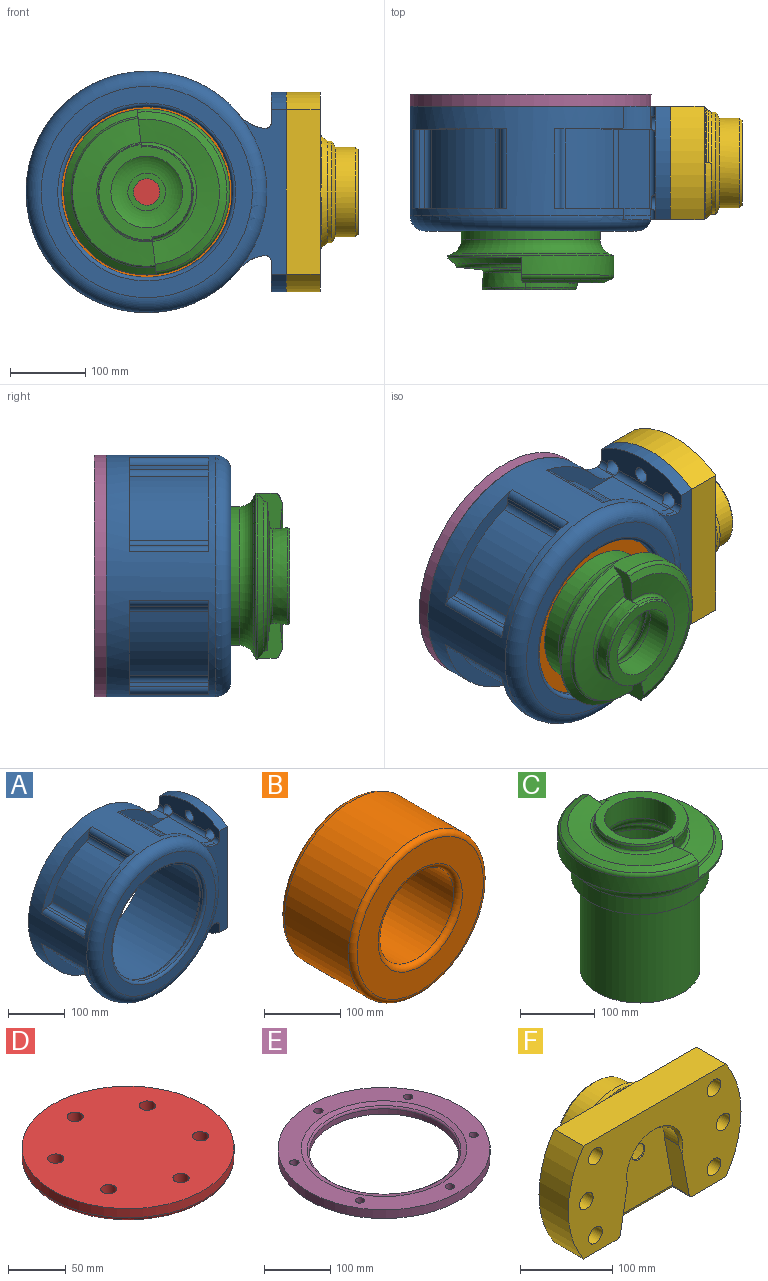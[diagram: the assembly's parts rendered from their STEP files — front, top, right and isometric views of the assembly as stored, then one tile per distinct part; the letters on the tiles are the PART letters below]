
ASSEMBLY  parts=6 mates=13
PART A: 99 faces, bbox 381.5x168.7x349.7 mm
  f0: cylinder r=30mm len=60mm, axis (1,0,0), area 6597.3mm2, adj f6,f71
  f1: plane 265x150mm, normal (1,0,0), area 30406.7mm2, adj f7,f8,f38,f39,f40,f61,f63,f65
  f2: plane 150x40.5mm, normal (-1,0,0), area 4307.7mm2, adj f4,f7,f8,f39,f65,f67,f70
  f3: plane 150x40.5mm, normal (-1,0,0), area 4307.7mm2, adj f5,f7,f8,f38,f61,f63,f69
  f4: cylinder r=8mm len=150mm, axis (0,-1,0), area 1467.6mm2, adj f2,f7,f8,f11,f12,f36,f41,f42
  f5: cylinder r=8mm len=150mm, axis (0,1,0), area 1467.6mm2, adj f3,f7,f8,f23,f24,f37,f44,f45
  f6: plane 80x80mm, normal (1,0,0), area 2199.1mm2, adj f0,f40
  f7: plane 345x320mm, normal (0,1,0), area 36954.8mm2, adj f1,f2,f3,f4,f5,f10,f14,f38
  f8: plane 221.75x66.5mm, normal (0,-1,0), area 6828.4mm2, adj f1,f2,f3,f4,f5,f13,f38,f39
  f9: cylinder r=140mm len=105mm, axis (0,1,0), area 8139.3mm2, adj f23,f24,f47,f53
  f10: cylinder r=160mm len=320mm, axis (0,1,0), area 51651.4mm2, adj f7,f11,f12,f13,f18,f19,f23,f24
  f11: plane 126.34x72.77mm, normal (0,1,0), area 2207.3mm2, adj f4,f10,f20,f21,f36,f43,f48,f55
  f12: plane 126.34x72.77mm, normal (0,-1,0), area 2207.3mm2, adj f4,f10,f20,f21,f36,f41,f48,f55
  f13: torus R=140mm, axis (0,1,0), area 29023.4mm2, adj f8,f10,f33,f42,f45
  f14: cylinder r=125mm len=250mm, axis (0,1,0), area 114668.1mm2, adj f7,f35
  f15: plane 105x5.55mm, normal (-1,0,0), area 582.5mm2, adj f18,f19,f57,f60
  f16: plane 105x5.55mm, normal (0,0,-1), area 582.5mm2, adj f18,f19,f58,f59
  f17: cylinder r=140mm len=105mm, axis (0,1,0), area 13099.5mm2, adj f18,f19,f59,f60
  f18: plane 124.77x124.77mm, normal (0,1,0), area 3098.8mm2, adj f10,f15,f16,f17,f57,f58,f59,f60
  f19: plane 124.77x124.77mm, normal (0,-1,0), area 3098.8mm2, adj f10,f15,f16,f17,f57,f58,f59,f60
  f20: cylinder r=140mm len=105mm, axis (0,1,0), area 8139.3mm2, adj f11,f12,f48,f56
  f21: plane 105x5.55mm, normal (1,0,0), area 582.5mm2, adj f11,f12,f55,f56
  f22: plane 105x5.55mm, normal (1,0,0), area 582.5mm2, adj f23,f24,f53,f54
  f23: plane 126.34x72.77mm, normal (0,1,0), area 2207.3mm2, adj f5,f9,f10,f22,f37,f46,f47,f53
  f24: plane 126.34x72.77mm, normal (0,-1,0), area 2207.3mm2, adj f5,f9,f10,f22,f37,f44,f47,f53
  f25: plane 105x5.55mm, normal (0,0,1), area 582.5mm2, adj f28,f29,f49,f52
  f26: plane 105x5.55mm, normal (-1,0,0), area 582.5mm2, adj f28,f29,f50,f51
  f27: cylinder r=140mm len=105mm, axis (0,1,0), area 13099.5mm2, adj f28,f29,f51,f52
  f28: plane 124.77x124.77mm, normal (0,1,0), area 3098.8mm2, adj f10,f25,f26,f27,f49,f50,f51,f52
  f29: plane 124.77x124.77mm, normal (0,-1,0), area 3098.8mm2, adj f10,f25,f26,f27,f49,f50,f51,f52
  f30: cylinder r=113mm len=226mm, axis (0,1,0), area 4260mm2, adj f31,f34
  f31: torus R=117mm, axis (0,1,0), area 4518.4mm2, adj f30,f32
  f32: plane 242x242mm, normal (0,1,0), area 2990.8mm2, adj f31,f35
  f33: plane 280x280mm, normal (0,-1,0), area 17831.7mm2, adj f13,f34
  f34: torus R=118mm, axis (0,1,0), area 5666mm2, adj f30,f33
  f35: torus R=121mm, axis (0,-1,0), area 4877.4mm2, adj f14,f32
  f36: plane 105x40.11mm, normal (0,0,-1), area 4211.2mm2, adj f4,f11,f12,f48
  f37: plane 105x40.11mm, normal (0,0,1), area 4211.2mm2, adj f5,f23,f24,f47
  f38: cylinder r=132.5mm len=150mm, axis (1,0,0), area 3189mm2, adj f1,f3,f7,f8
  f39: cylinder r=132.5mm len=150mm, axis (1,0,0), area 3189mm2, adj f1,f2,f7,f8
  f40: cylinder r=40mm len=80mm, axis (1,0,0), area 5026.5mm2, adj f1,f6
  f41: cylinder r=50mm len=35.14mm, axis (0,1,0), area 1217.5mm2, adj f4,f7,f10,f12
  f42: bspline ~40.41x26.95mm, area 251.6mm2, adj f4,f8,f13,f43
  f43: cylinder r=50mm len=35.14mm, axis (0,1,0), area 405.8mm2, adj f4,f10,f11,f42
  f44: cylinder r=50mm len=35.14mm, axis (0,1,0), area 1217.5mm2, adj f5,f7,f10,f24
  f45: bspline ~40.41x26.95mm, area 251.6mm2, adj f5,f8,f13,f46
  f46: cylinder r=50mm len=35.14mm, axis (0,1,0), area 405.8mm2, adj f5,f10,f23,f45
  f47: cylinder r=10mm len=105mm, axis (0,1,0), area 938.2mm2, adj f9,f23,f24,f37
  f48: cylinder r=10mm len=105mm, axis (0,1,0), area 938.2mm2, adj f11,f12,f20,f36
  f49: cylinder r=10mm len=105mm, axis (0,1,0), area 1437.9mm2, adj f10,f25,f28,f29
  f50: cylinder r=10mm len=105mm, axis (0,1,0), area 1437.9mm2, adj f10,f26,f28,f29
  f51: cylinder r=10mm len=105mm, axis (0,1,0), area 1292.5mm2, adj f26,f27,f28,f29
  f52: cylinder r=10mm len=105mm, axis (0,1,0), area 1292.5mm2, adj f25,f27,f28,f29
  f53: cylinder r=10mm len=105mm, axis (0,1,0), area 1292.5mm2, adj f9,f22,f23,f24
  f54: cylinder r=10mm len=105mm, axis (0,1,0), area 1437.9mm2, adj f10,f22,f23,f24
  f55: cylinder r=10mm len=105mm, axis (0,1,0), area 1437.9mm2, adj f10,f11,f12,f21
  f56: cylinder r=10mm len=105mm, axis (0,1,0), area 1292.5mm2, adj f11,f12,f20,f21
  f57: cylinder r=10mm len=105mm, axis (0,1,0), area 1437.9mm2, adj f10,f15,f18,f19
  f58: cylinder r=10mm len=105mm, axis (0,1,0), area 1437.9mm2, adj f10,f16,f18,f19
  f59: cylinder r=10mm len=105mm, axis (0,1,0), area 1292.5mm2, adj f16,f17,f18,f19
  f60: cylinder r=10mm len=105mm, axis (0,1,0), area 1292.5mm2, adj f15,f17,f18,f19
  f61: cylinder r=10.5mm len=25mm, axis (1,0,0), area 1455.7mm2, adj f1,f3,f5,f62
  f62: plane 16.73x4.15mm, normal (1,0,0), area 48.5mm2, adj f5,f61
  f63: cylinder r=10.5mm len=25mm, axis (1,0,0), area 1455.7mm2, adj f1,f3,f5,f64
  f64: plane 16.73x4.15mm, normal (1,0,0), area 48.5mm2, adj f5,f63
  f65: cylinder r=10.5mm len=25mm, axis (1,0,0), area 1455.7mm2, adj f1,f2,f4,f66
  f66: plane 16.73x4.15mm, normal (1,0,0), area 48.5mm2, adj f4,f65
  f67: cylinder r=10.5mm len=25mm, axis (1,0,0), area 1455.7mm2, adj f1,f2,f4,f68
  f68: plane 16.73x4.15mm, normal (1,0,0), area 48.5mm2, adj f4,f67
  f69: cylinder r=10.5mm len=21mm, axis (1,0,0), area 1319.5mm2, adj f1,f3
  f70: cylinder r=10.5mm len=21mm, axis (1,0,0), area 1319.5mm2, adj f1,f2
  f71: plane 100x80mm, normal (-1,0,0), area 5172.6mm2, adj f0,f74,f75,f79,f80
  f72: cylinder r=10mm len=100mm, axis (0,-1,0), area 1840.7mm2, adj f73,f78,f79,f80
  f73: plane 100x15.43mm, normal (0,0,1), area 1543.2mm2, adj f72,f74,f79,f80
  f74: cylinder r=10mm len=100mm, axis (0,-1,0), area 1570.8mm2, adj f71,f73,f79,f80
  f75: cylinder r=10mm len=100mm, axis (0,-1,0), area 1570.8mm2, adj f71,f76,f79,f80
  f76: plane 100x15.43mm, normal (0,0,-1), area 1543.2mm2, adj f75,f77,f79,f80
  f77: cylinder r=10mm len=100mm, axis (0,-1,0), area 1840.7mm2, adj f76,f78,f79,f80
  f78: cylinder r=140mm len=100mm, axis (0,-1,0), area 7558.1mm2, adj f72,f77,f79,f80
  f79: plane 100x35.43mm, normal (0,-1,0), area 3176.4mm2, adj f71,f72,f73,f74,f75,f76,f77,f78
  f80: plane 100x35.43mm, normal (0,1,0), area 3176.4mm2, adj f71,f72,f73,f74,f75,f76,f77,f78
  f81: cylinder r=6.6mm len=15mm, axis (0,1,0), area 622mm2, adj f82,f83
  f82: cone r=0mm half-angle=59deg, axis (0,1,0), area 159.7mm2, adj f81
  f83: cone r=6.6mm half-angle=45deg, axis (0,1,0), area 63.1mm2, adj f7,f81
  f84: cylinder r=6.6mm len=15mm, axis (0,1,0), area 622mm2, adj f85,f86
  f85: cone r=0mm half-angle=59deg, axis (0,1,0), area 159.7mm2, adj f84
  f86: cone r=6.6mm half-angle=45deg, axis (0,1,0), area 63.1mm2, adj f7,f84
  f87: cylinder r=6.6mm len=15mm, axis (0,1,0), area 622mm2, adj f88,f89
  f88: cone r=0mm half-angle=59deg, axis (0,1,0), area 159.7mm2, adj f87
  f89: cone r=6.6mm half-angle=45deg, axis (0,1,0), area 63.1mm2, adj f7,f87
  f90: cylinder r=6.6mm len=15mm, axis (0,1,0), area 622mm2, adj f91,f92
  f91: cone r=0mm half-angle=59deg, axis (0,1,0), area 159.7mm2, adj f90
  f92: cone r=6.6mm half-angle=45deg, axis (0,1,0), area 63.1mm2, adj f7,f90
  f93: cylinder r=6.6mm len=15mm, axis (0,1,0), area 622mm2, adj f94,f95
  f94: cone r=0mm half-angle=59deg, axis (0,1,0), area 159.7mm2, adj f93
  f95: cone r=6.6mm half-angle=45deg, axis (0,1,0), area 63.1mm2, adj f7,f93
  f96: cylinder r=6.6mm len=15mm, axis (0,1,0), area 622mm2, adj f97,f98
  f97: cone r=0mm half-angle=59deg, axis (0,1,0), area 159.7mm2, adj f96
  f98: cone r=6.6mm half-angle=45deg, axis (0,1,0), area 63.1mm2, adj f7,f96
PART B: 8 faces, bbox 270.6x134x270.6 mm
  f0: cylinder r=70mm len=140mm, axis (0,1,0), area 51899.1mm2, adj f4,f6
  f1: cylinder r=125mm len=250mm, axis (0,1,0), area 92677mm2, adj f5,f7
  f2: plane 234x234mm, normal (0,-1,0), area 23891.8mm2, adj f6,f7
  f3: plane 234x234mm, normal (0,1,0), area 23891.8mm2, adj f4,f5
  f4: torus R=78mm, axis (0,-1,0), area 5756.5mm2, adj f0,f3
  f5: torus R=117mm, axis (0,-1,0), area 9640.1mm2, adj f1,f3
  f6: torus R=78mm, axis (0,-1,0), area 5756.5mm2, adj f0,f2
  f7: torus R=117mm, axis (0,-1,0), area 9640.1mm2, adj f1,f2
PART C: 52 faces, bbox 242.5x242.5x250 mm
  f0: plane 11.85x4.5mm, normal (-1,0,0), area 30.8mm2, adj f2,f43,f45,f46,f49,f50
  f1: plane 11.85x4.5mm, normal (-1,0,0), area 30.8mm2, adj f2,f43,f45,f46,f49,f50
  f2: plane 126.72x123.34mm, normal (0,0,1), area 4869.3mm2, adj f0,f1,f3,f49,f50
  f3: cylinder r=47.5mm len=95mm, axis (0,0,1), area 9960.1mm2, adj f2,f7
  f4: plane 47.43x32.63mm, normal (1,0,0), area 883.5mm2, adj f5,f6,f41,f42,f43,f44,f46,f47
  f5: cone r=62mm half-angle=84.3deg, axis (0,0,-1), area 8363.5mm2, adj f4,f40,f42,f44
  f6: cylinder r=110mm len=220mm, axis (0,0,1), area 9891.7mm2, adj f4,f22,f40,f41,f51
  f7: torus R=63.5mm, axis (0,0,1), area 3876.4mm2, adj f3,f8
  f8: cone r=60.31mm half-angle=45deg, axis (0,0,-1), area 4062.3mm2, adj f7,f9
  f9: torus R=49mm, axis (0,0,1), area 5006.3mm2, adj f8,f10
  f10: cylinder r=65mm len=130mm, axis (0,0,1), area 51407.2mm2, adj f9,f11
  f11: torus R=25mm, axis (0,0,1), area 19922.7mm2, adj f10,f12
  f12: plane 50x50mm, normal (0,0,1), area 1001.4mm2, adj f11,f13
  f13: cylinder r=17.5mm len=35mm, axis (0,0,1), area 2110.7mm2, adj f12,f23
  f14: plane 90x90mm, normal (0,0,-1), area 5041.5mm2, adj f15,f23
  f15: cylinder r=45mm len=90mm, axis (0,0,1), area 1413.7mm2, adj f14,f16
  f16: plane 160x160mm, normal (0,0,-1), area 13067.8mm2, adj f15,f17,f24,f27,f29,f31,f33,f35
  f17: cylinder r=80mm len=160mm, axis (0,0,1), area 73084mm2, adj f16,f18
  f18: torus R=86mm, axis (0,0,1), area 4025.4mm2, adj f17,f19
  f19: cone r=84.45mm half-angle=75deg, axis (0,0,1), area 4334.5mm2, adj f18,f20
  f20: cylinder r=92mm len=184mm, axis (0,0,1), area 14826.9mm2, adj f19,f21
  f21: torus R=112mm, axis (0,0,1), area 13689mm2, adj f20,f22
  f22: cone r=110mm half-angle=65deg, axis (0,0,1), area 4776.3mm2, adj f6,f21
  f23: cone r=20.5mm half-angle=75deg, axis (0,0,-1), area 370.8mm2, adj f13,f14
  f24: cylinder r=5.25mm len=19mm, axis (0,0,-1), area 626.7mm2, adj f16,f25
  f25: cone r=0mm half-angle=59deg, axis (0,0,-1), area 101mm2, adj f24
  f26: cone r=0mm half-angle=59deg, axis (0,0,-1), area 101mm2, adj f27
  f27: cylinder r=5.25mm len=19mm, axis (0,0,-1), area 626.7mm2, adj f16,f26
  f28: cone r=0mm half-angle=59deg, axis (0,0,-1), area 101mm2, adj f29
  f29: cylinder r=5.25mm len=19mm, axis (0,0,-1), area 626.7mm2, adj f16,f28
  f30: cone r=0mm half-angle=59deg, axis (0,0,-1), area 101mm2, adj f31
  f31: cylinder r=5.25mm len=19mm, axis (0,0,-1), area 626.7mm2, adj f16,f30
  f32: cone r=0mm half-angle=59deg, axis (0,0,-1), area 101mm2, adj f33
  f33: cylinder r=5.25mm len=19mm, axis (0,0,-1), area 626.7mm2, adj f16,f32
  f34: cone r=0mm half-angle=59deg, axis (0,0,-1), area 101mm2, adj f35
  f35: cylinder r=5.25mm len=19mm, axis (0,0,-1), area 626.7mm2, adj f16,f34
  f36: cylinder r=5mm len=10mm, axis (0,0,-1), area 314.2mm2, adj f16,f37
  f37: plane 10x10mm, normal (0,0,-1), area 78.5mm2, adj f36
  f38: cylinder r=5mm len=10mm, axis (0,0,-1), area 314.2mm2, adj f16,f39
  f39: plane 10x10mm, normal (0,0,-1), area 78.5mm2, adj f38
  f40: plane 47.43x32.63mm, normal (1,0,0), area 883.5mm2, adj f5,f6,f41,f42,f43,f44,f46,f47
  f41: cone r=110mm half-angle=51deg, axis (0,0,-1), area 4003.1mm2, adj f4,f6,f40,f42
  f42: torus R=104.37mm, axis (0,0,1), area 1633.8mm2, adj f4,f5,f40,f41
  f43: cone r=62.19mm half-angle=5.7deg, axis (0,0,1), area 3814.8mm2, adj f0,f1,f4,f40,f44,f49
  f44: torus R=66.57mm, axis (0,0,1), area 1259mm2, adj f4,f5,f40,f43
  f45: cone r=61.69mm half-angle=5.7deg, axis (0,0,-1), area 1130.6mm2, adj f0,f1,f46,f50
  f46: torus R=65.67mm, axis (0,0,-1), area 1251.3mm2, adj f0,f1,f4,f40,f45,f47
  f47: cone r=66.07mm half-angle=84.3deg, axis (0,0,1), area 7784.9mm2, adj f4,f40,f46,f48
  f48: cone r=110mm half-angle=65.7deg, axis (0,0,-1), area 3513.6mm2, adj f4,f40,f47,f51
  f49: cone r=63.36mm half-angle=19.4deg, axis (0,0,-1), area 683.3mm2, adj f0,f1,f2,f43
  f50: cone r=61.11mm half-angle=20.7deg, axis (0,0,-1), area 607mm2, adj f0,f1,f2,f45
  f51: torus R=104mm, axis (0,0,1), area 2351mm2, adj f4,f6,f40,f48
PART D: 15 faces, bbox 199.2x199.2x16 mm
  f0: cylinder r=45mm len=90mm, axis (0,0,1), area 1131mm2, adj f7,f8
  f1: plane 160x160mm, normal (0,0,-1), area 12242.8mm2, adj f2,f8,f9,f10,f11,f12,f13,f14
  f2: cone r=80mm half-angle=75deg, axis (0,0,1), area 4967.4mm2, adj f1,f3
  f3: torus R=88mm, axis (0,0,1), area 2992.2mm2, adj f2,f4
  f4: cylinder r=92mm len=184mm, axis (0,0,1), area 5616mm2, adj f3,f5
  f5: plane 184x184mm, normal (0,0,1), area 25666.8mm2, adj f4,f9,f10,f11,f12,f13,f14
  f6: plane 86x86mm, normal (0,0,-1), area 5808.8mm2, adj f7
  f7: torus R=43mm, axis (0,0,1), area 873.9mm2, adj f0,f6
  f8: cone r=47mm half-angle=45deg, axis (0,0,-1), area 817.5mm2, adj f0,f1
  f9: cylinder r=7mm len=16mm, axis (0,0,-1), area 703.7mm2, adj f1,f5
  f10: cylinder r=7mm len=16mm, axis (0,0,-1), area 703.7mm2, adj f1,f5
  f11: cylinder r=7mm len=16mm, axis (0,0,-1), area 703.7mm2, adj f1,f5
  f12: cylinder r=7mm len=16mm, axis (0,0,-1), area 703.7mm2, adj f1,f5
  f13: cylinder r=7mm len=16mm, axis (0,0,-1), area 703.7mm2, adj f1,f5
  f14: cylinder r=7mm len=16mm, axis (0,0,-1), area 703.7mm2, adj f1,f5
PART E: 12 faces, bbox 320x320x16 mm
  f0: cylinder r=113mm len=226mm, axis (0,0,1), area 6897.9mm2, adj f1,f5
  f1: plane 320x320mm, normal (0,0,-1), area 39386.1mm2, adj f0,f2,f6,f7,f8,f9,f10,f11
  f2: cylinder r=160mm len=320mm, axis (0,0,1), area 16085mm2, adj f1,f3
  f3: plane 320x320mm, normal (0,0,1), area 30413.8mm2, adj f2,f4,f6,f7,f8,f9,f10,f11
  f4: cone r=125mm half-angle=75deg, axis (0,0,1), area 7081.1mm2, adj f3,f5
  f5: torus R=117mm, axis (0,0,1), area 3752mm2, adj f0,f4
  f6: cylinder r=7mm len=16mm, axis (0,0,1), area 703.7mm2, adj f1,f3
  f7: cylinder r=7mm len=16mm, axis (0,0,1), area 703.7mm2, adj f1,f3
  f8: cylinder r=7mm len=16mm, axis (0,0,1), area 703.7mm2, adj f1,f3
  f9: cylinder r=7mm len=16mm, axis (0,0,1), area 703.7mm2, adj f1,f3
  f10: cylinder r=7mm len=16mm, axis (0,0,1), area 703.7mm2, adj f1,f3
  f11: cylinder r=7mm len=16mm, axis (0,0,1), area 703.7mm2, adj f1,f3
PART F: 56 faces, bbox 265x95x166.1 mm
  f0: cylinder r=10.5mm len=43mm, axis (0,1,0), area 2836.9mm2, adj f13,f44
  f1: cylinder r=10.5mm len=43mm, axis (0,1,0), area 2836.9mm2, adj f13,f43
  f2: cylinder r=10.5mm len=43mm, axis (0,1,0), area 2836.9mm2, adj f13,f40
  f3: plane 150x116.21mm, normal (0,1,0), area 5693.8mm2, adj f6,f8,f12,f27,f30,f33,f46,f48
  f4: cone r=67.5mm half-angle=36.9deg, axis (0,-1,0), area 2247.8mm2, adj f20,f27,f28,f29,f30,f31,f32
  f5: plane 150x116.21mm, normal (0,1,0), area 5693.8mm2, adj f6,f7,f8,f28,f31,f36,f41,f42
  f6: plane 218.46x45mm, normal (0,0,-1), area 6369.9mm2, adj f3,f5,f7,f12,f13,f34,f35,f53
  f7: cylinder r=132.5mm len=150mm, axis (0,1,0), area 7175.2mm2, adj f5,f6,f8,f13
  f8: plane 218.46x45mm, normal (0,0,1), area 9830.7mm2, adj f3,f5,f7,f12,f13,f29,f32
  f9: cylinder r=10.5mm len=43mm, axis (0,1,0), area 2836.9mm2, adj f13,f47
  f10: cylinder r=10.5mm len=43mm, axis (0,1,0), area 2836.9mm2, adj f13,f49
  f11: cylinder r=10.5mm len=43mm, axis (0,1,0), area 2836.9mm2, adj f13,f51
  f12: cylinder r=132.5mm len=150mm, axis (0,1,0), area 7175.2mm2, adj f3,f6,f8,f13
  f13: plane 265x150mm, normal (0,-1,0), area 25475.2mm2, adj f0,f1,f2,f6,f7,f8,f9,f10
  f14: plane 110x105.2mm, normal (0,-1,0), area 8678mm2, adj f15,f16,f17,f52,f55
  f15: cylinder r=40mm len=80mm, axis (0,-1,0), area 2764.6mm2, adj f14,f16,f17,f18
  f16: plane 70.89x25.08mm, normal (0.98,0,-0.18), area 1783.4mm2, adj f13,f14,f15,f18,f53,f55
  f17: plane 70.89x25.08mm, normal (-0.98,0,-0.18), area 1783.4mm2, adj f13,f14,f15,f18,f54,f55
  f18: cone r=40mm half-angle=45deg, axis (0,-1,0), area 601.5mm2, adj f13,f15,f16,f17
  f19: cone r=59.5mm half-angle=60deg, axis (0,-1,0), area 3685.6mm2, adj f20,f23
  f20: cylinder r=67.5mm len=135mm, axis (0,1,0), area 2282.2mm2, adj f4,f19,f24
  f21: cylinder r=49.5mm len=99mm, axis (0,1,0), area 18039mm2, adj f22,f38
  f22: plane 113x113mm, normal (0,1,0), area 2331.1mm2, adj f21,f39
  f23: cylinder r=59.5mm len=119mm, axis (0,1,0), area 10093.9mm2, adj f19,f39
  f24: cone r=67.5mm half-angle=28.1deg, axis (0,-1,0), area 1154.7mm2, adj f20,f25,f27,f28
  f25: torus R=74.87mm, axis (0,-1,0), area 725.6mm2, adj f24,f26,f27,f28
  f26: cone r=75mm half-angle=51.4deg, axis (0,-1,0), area 567.4mm2, adj f25,f27,f28,f33,f34,f35,f36
  f27: plane 10x10mm, normal (0,0,-1), area 8.4mm2, adj f3,f4,f24,f25,f26,f30,f33
  f28: plane 10x10mm, normal (0,0,-1), area 8.4mm2, adj f4,f5,f24,f25,f26,f31,f36
  f29: bspline ~22.8x4.69mm, area 43.3mm2, adj f4,f8,f30
  f30: torus R=77.5mm, axis (0,-1,0), area 459.8mm2, adj f3,f4,f27,f29
  f31: torus R=77.5mm, axis (0,-1,0), area 459.8mm2, adj f4,f5,f28,f32
  f32: bspline ~22.8x4.69mm, area 43.3mm2, adj f4,f8,f31
  f33: torus R=76.75mm, axis (0,-1,0), area 343.1mm2, adj f3,f26,f27,f34
  f34: bspline ~18.64x3.54mm, area 26.6mm2, adj f6,f26,f33
  f35: bspline ~18.64x3.54mm, area 26.6mm2, adj f6,f26,f36
  f36: torus R=76.75mm, axis (0,-1,0), area 343.1mm2, adj f5,f26,f28,f35
  f37: plane 79x79mm, normal (0,1,0), area 4584.4mm2, adj f38,f52
  f38: torus R=39.5mm, axis (0,1,0), area 4526.8mm2, adj f21,f37
  f39: cone r=56.5mm half-angle=45deg, axis (0,-1,0), area 1546.1mm2, adj f22,f23
  f40: plane 40x40mm, normal (0,1,0), area 910.3mm2, adj f2,f41
  f41: cylinder r=20mm len=40mm, axis (0,1,0), area 251.3mm2, adj f5,f40
  f42: cylinder r=20mm len=40mm, axis (0,1,0), area 251.3mm2, adj f5,f43
  f43: plane 40x40mm, normal (0,1,0), area 910.3mm2, adj f1,f42
  f44: plane 40x40mm, normal (0,1,0), area 910.3mm2, adj f0,f45
  f45: cylinder r=20mm len=40mm, axis (0,1,0), area 251.3mm2, adj f5,f44
  f46: cylinder r=20mm len=40mm, axis (0,1,0), area 251.3mm2, adj f3,f47
  f47: plane 40x40mm, normal (0,1,0), area 910.3mm2, adj f9,f46
  f48: cylinder r=20mm len=40mm, axis (0,1,0), area 251.3mm2, adj f3,f49
  f49: plane 40x40mm, normal (0,1,0), area 910.3mm2, adj f10,f48
  f50: cylinder r=20mm len=40mm, axis (0,1,0), area 251.3mm2, adj f3,f51
  f51: plane 40x40mm, normal (0,1,0), area 910.3mm2, adj f11,f50
  f52: cylinder r=10.05mm len=20.1mm, axis (0,1,0), area 126.3mm2, adj f14,f37
  f53: cylinder r=5mm len=30mm, axis (0,-1,0), area 188.3mm2, adj f6,f13,f16,f55
  f54: cylinder r=5mm len=30mm, axis (0,1,0), area 188.3mm2, adj f6,f13,f17,f55
  f55: cylinder r=5mm len=115.36mm, axis (-1,0,0), area 856mm2, adj f6,f14,f16,f17,f53,f54
PLACE A t=(-87.99,-72.92,-63.91)mm fixed
PLACE B rot(axis=(0,-1,0),90deg) t=(-87.99,-80.92,-63.91)mm
PLACE C rot(axis=(0.04,0.71,-0.71),175.3deg) t=(-87.99,9.28,-63.91)mm
PLACE D rot(axis=(-0.23,0.69,0.69),154.3deg) t=(-87.99,1.28,-63.91)mm
PLACE E rot(axis=(0.77,0.45,-0.45),104.5deg) t=(-87.99,18.08,-63.91)mm
PLACE F rot(axis=(0.58,0.58,-0.58),120deg) t=(119.51,-72.92,-63.91)mm
MATE cylindrical C.f3 <-> D.f0  axis (0,-1,0) through (-87.99,6.78,-63.91)mm
MATE planar D.f0 <-> C.f45  axis (0,-1,0) through (-87.99,9.28,-63.91)mm
MATE cylindrical C.f28 <-> D.f12  axis (0,1,0) through (-126.78,-5.22,-11.76)mm
MATE planar E.f0 <-> A.f7  axis (0,-1,0) through (-87.99,2.08,-63.91)mm
MATE planar B.f0 <-> A.f9  axis (0,-1,0) through (-87.99,-147.92,-63.91)mm
MATE cylindrical A.f9 <-> B.f0  axis (0,1,0) through (-87.99,-70.92,-63.91)mm
MATE cylindrical C.f3 <-> B.f0  axis (0,-1,0) through (-87.99,-68.41,-63.91)mm
MATE planar C.f3 <-> B.f0  axis (0,-1,0) through (-87.99,-147.92,-63.91)mm
MATE cylindrical A.f65 <-> F.f0  axis (1,0,0) through (84.51,-125.42,-154.85)mm
MATE cylindrical E.f0 <-> A.f9  axis (0,-1,0) through (-87.99,13.22,-63.91)mm
MATE cylindrical E.f6 <-> A.f87  axis (0,-1,0) through (33.26,10.08,6.09)mm
MATE cylindrical F.f4 <-> A.f38  axis (-1,0,0) through (111.01,-72.92,-63.91)mm
MATE planar A.f39 <-> F.f13  axis (1,0,0) through (97.01,-72.92,-63.91)mm
